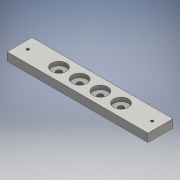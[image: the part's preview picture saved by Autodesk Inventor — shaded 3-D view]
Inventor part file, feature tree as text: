
AUTODESK INVENTOR PART (.ipt)
format: ipt  version: 2016 (Build 200138000, 138)  size: 122,368 bytes
history: native  units: mm
features: sketch x3, hole x2, extrude x1
ambient origin geometry x8: Origin, YZ Plane, XZ Plane, XY Plane, X Axis, Y Axis, Z Axis, Center Point
bodies: Solid1 (feature_tree)
feature tree (6):
  extrude  "Extrusion1"  Depth=170.0mm
  hole  "Hole1"  [1 undecoded]
  hole  "Hole2"  [1 undecoded]
  sketch  "Sketch1"  dims[d0=30.0mm d1=170.0mm]
  sketch  "Sketch2"  dims[d2=85.0mm d3=15.0mm]
  sketch  "Sketch3"  dims[d4=10.0mm d5=0.0mm d9=6.6mm d10=6.0mm d11=18.0mm d12=4.8mm d13=90.0deg d14=8.0mm d15=20.594885mm d16=150.0mm d17=75.0mm d19=3.242mm d20=8.0mm d21=19.05mm d22=4.775mm d23=90.0deg d24=11.8mm d25=20.594885mm d30=25.0mm d31=25.0mm d32=25.0mm d33=12.5mm]
note: 2 required parameter values undecoded (feature->parameter linkage not recoverable at this tier; creation-order binding heuristic only, values carry confidence <= 0.55)
